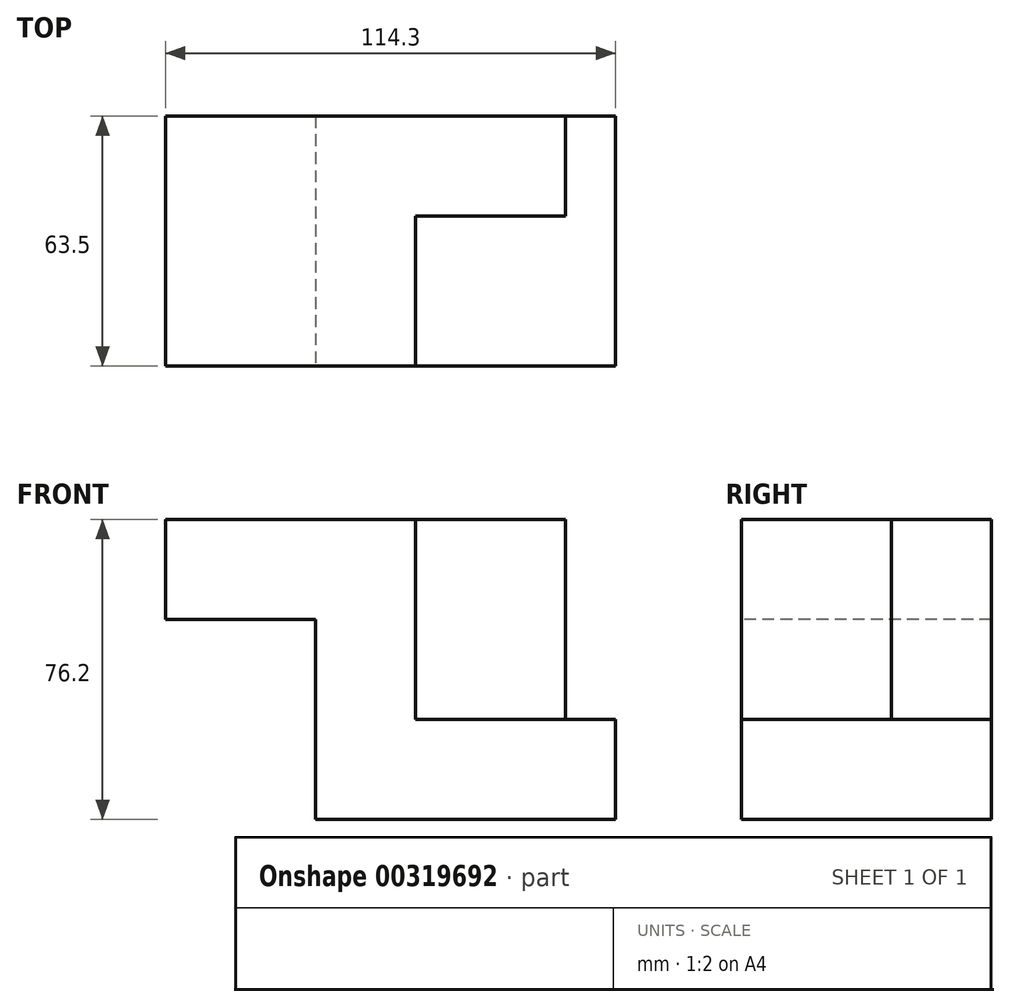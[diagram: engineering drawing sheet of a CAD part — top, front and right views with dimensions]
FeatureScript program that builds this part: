
annotation { "Feature Type Name" : "Feature", "Feature Type Description" : "" }
export const myFeature = defineFeature(function(context is Context, id is Id, definition is map)
    precondition{}
    {
        {
            var Q0;
            Q0=qCreatedBy(makeId("Front.planeOp"),FACE);
            var sketch = newSketch(context, id + "F0", { "sketchPlane" : qUnion([Q0])});
            skLineSegment(sketch, "E0", {"start": v(-31.87, -6.71) * mm, "end": v(44.33, -6.71) * mm});
            skLineSegment(sketch, "E1", {"start": v(44.33, -6.71) * mm, "end": v(44.33, 18.69) * mm});
            skLineSegment(sketch, "E2", {"start": v(44.33, 18.69) * mm, "end": v(-6.47, 18.69) * mm});
            skLineSegment(sketch, "E3", {"start": v(-6.47, 18.69) * mm, "end": v(-6.47, 69.49) * mm});
            skLineSegment(sketch, "E4", {"start": v(-6.47, 69.49) * mm, "end": v(-69.97, 69.49) * mm});
            skLineSegment(sketch, "E5", {"start": v(-69.97, 69.49) * mm, "end": v(-69.97, 44.09) * mm});
            skLineSegment(sketch, "E6", {"start": v(-69.97, 44.09) * mm, "end": v(-31.87, 44.09) * mm});
            skLineSegment(sketch, "E7", {"start": v(-31.87, 44.09) * mm, "end": v(-31.87, -6.71) * mm});
            skSolve(sketch);
        }
        {
            var Q0;
            Q0=makeQuery(id+"F0.imprint","IMPRINT",FACE,{"disambiguationData":[TD([[makeQuery(id+"F0.imprint","IMPRINT",EDGE,{"derivedFrom":sQuery(id+"F0.wireOp",EDGE,"E0")}),1.0]])]});
            extrude(context, id + "F1", {"entities" : qUnion([Q0]), "oppositeDirection" : true, "depth" : 63.5 * mm});
        }
        {
            var Q0;
            Q0=makeQuery(id+"F1.opExtrude","SWEPT_FACE",FACE,{"disambiguationData":[OSD([sQuery(id+"F0.wireOp",EDGE,"E2")])]});
            var sketch = newSketch(context, id + "F2", { "sketchPlane" : qUnion([Q0])});
            skLineSegment(sketch, "E8", {"start": v(-6.47, 63.5) * mm, "end": v(31.63, 63.5) * mm});
            skLineSegment(sketch, "E9", {"start": v(31.63, 63.5) * mm, "end": v(31.63, 38.1) * mm});
            skLineSegment(sketch, "E10", {"start": v(31.63, 38.1) * mm, "end": v(-6.47, 38.1) * mm});
            skSolve(sketch);
        }
        {
            var Q0;
            {var subQ0=sQuery(id+"F2.wireOp",EDGE,"E8");Q0=makeQuery(id+"F2.imprint","IMPRINT",FACE,{"disambiguationData":[TD([[makeQuery(id+"F2.imprint","IMPRINT",EDGE,{"derivedFrom":subQ0}),1.0]])]});}
            extrude(context, id + "F3", {"entities" : qUnion([Q0]), "operationType" : NewBodyOperationType.ADD, "depth" : 50.8 * mm});
        }
    });
